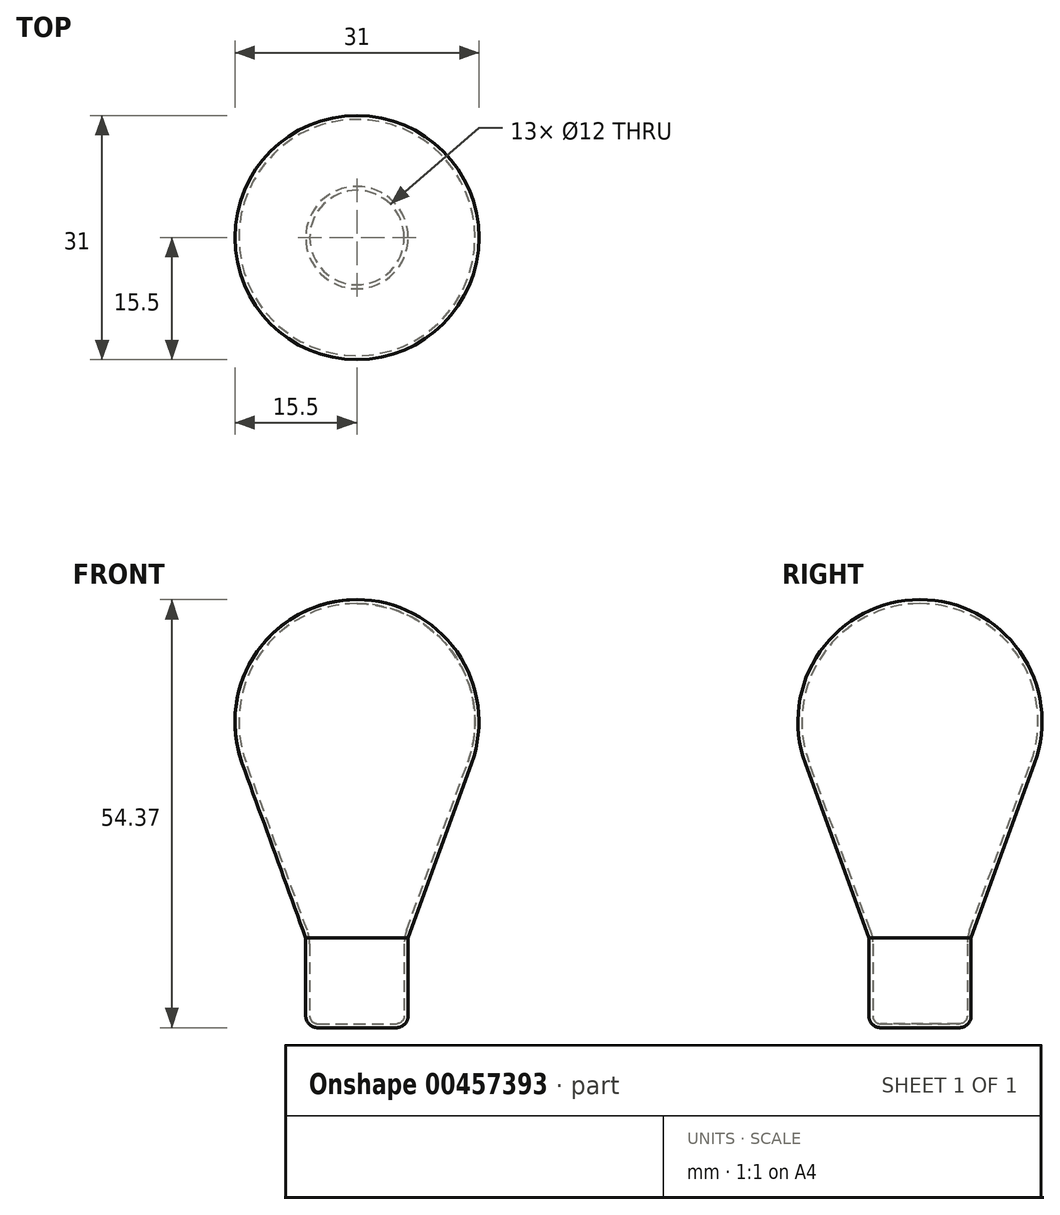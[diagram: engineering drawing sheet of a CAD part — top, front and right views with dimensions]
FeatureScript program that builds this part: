
annotation { "Feature Type Name" : "Feature", "Feature Type Description" : "" }
export const myFeature = defineFeature(function(context is Context, id is Id, definition is map)
    precondition{}
    {
        {
            var Q0;
            Q0=qCreatedBy(makeId("Front.planeOp"),FACE);
            var sketch = newSketch(context, id + "F0", { "sketchPlane" : qUnion([Q0])});
            skArc(sketch, "E0", {"start": v(0, 42.37) * mm, "mid": v(-12.29, 35.98) * mm, "end": v(-14.1, 22.24) * mm});
            skLineSegment(sketch, "E1", {"start": v(0, 0) * mm, "end": v(0, -0.5) * mm});
            skLineSegment(sketch, "E2", {"start": v(-6.3, 0.83) * mm, "end": v(-14.1, 22.24) * mm});
            skLineSegment(sketch, "E3", {"start": v(-6, -0.88) * mm, "end": v(-6, -10) * mm});
            skLineSegment(sketch, "E4", {"start": v(-5, -11) * mm, "end": v(0, -11) * mm});
            skPoint(sketch, "E5.visualSharp", {"position": v(-6, -11) * mm});
            skArc(sketch, "E5.filletArc", {"start": v(-6, -10) * mm, "mid": v(-5.7, -10.7) * mm, "end": v(-5, -11) * mm});
            skPoint(sketch, "E6.visualSharp", {"position": v(-6, 0) * mm});
            skArc(sketch, "E6.filletArc", {"start": v(-6, -0.88) * mm, "mid": v(-6.08, -0.01) * mm, "end": v(-6.3, 0.83) * mm});
            skLineSegment(sketch, "E7.0", {"start": v(-5, -11.5) * mm, "end": v(0, -11.5) * mm});
            skArc(sketch, "E7.1", {"start": v(0, 42.87) * mm, "mid": v(-12.7, 36.26) * mm, "end": v(-14.57, 22.07) * mm});
            skLineSegment(sketch, "E7.2", {"start": v(-6.5, -0.09) * mm, "end": v(-14.57, 22.07) * mm});
            skLineSegment(sketch, "E7.3", {"start": v(-6.5, -0.09) * mm, "end": v(-6.5, -10) * mm});
            skArc(sketch, "E7.4", {"start": v(-6.5, -10) * mm, "mid": v(-6.06, -11.06) * mm, "end": v(-5, -11.5) * mm});
            skLineSegment(sketch, "E8", {"start": v(0, -11.5) * mm, "end": v(0, -11) * mm});
            skLineSegment(sketch, "E9", {"start": v(0, 42.87) * mm, "end": v(0, 42.37) * mm});
            skSolve(sketch);
        }
        {
            var Q0;
            Q0=qCreatedBy(makeId("Front.planeOp"),FACE);
            var sketch = newSketch(context, id + "F1", { "sketchPlane" : qUnion([Q0])});
            skLineSegment(sketch, "E10", {"start": v(0, 0) * mm, "end": v(0, 87) * mm, "construction": true});
            skSolve(sketch);
        }
        {
            var Q0;
            Q0=makeQuery(id+"F0.imprint","IMPRINT",FACE,{"disambiguationData":[TD([[makeQuery(id+"F0.imprint","IMPRINT",EDGE,{"derivedFrom":sQuery(id+"F0.wireOp",EDGE,"E0")}),-1.0]])]});
            var Q1;
            Q1=sQuery(id+"F1.wireOp",EDGE,"E10");
            revolve(context, id + "F2", {"entities" : qUnion([Q0]), "axis" : qUnion([Q1]), "revolveType" : RevolveType.FULL});
        }
    });
